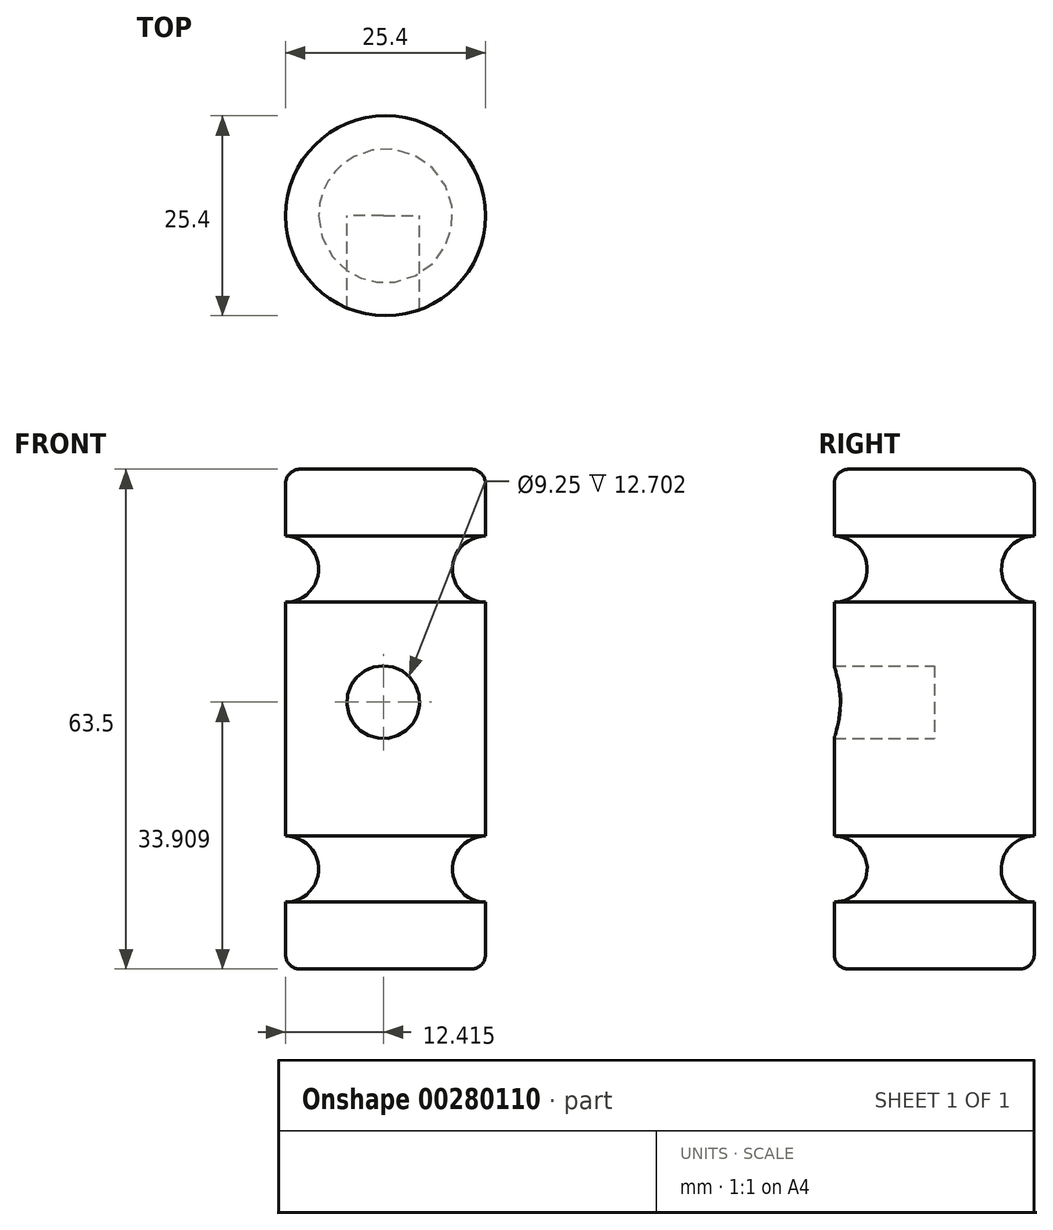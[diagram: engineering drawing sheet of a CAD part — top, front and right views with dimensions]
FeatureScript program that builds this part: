
annotation { "Feature Type Name" : "Feature", "Feature Type Description" : "" }
export const myFeature = defineFeature(function(context is Context, id is Id, definition is map)
    precondition{}
    {
        {
            var Q0;
            Q0=qCreatedBy(makeId("Front.planeOp"),FACE);
            var sketch = newSketch(context, id + "F0", { "sketchPlane" : qUnion([Q0])});
            skLineSegment(sketch, "E0.bottom", {"start": v(0, 0) * mm, "end": v(-12.7, 0) * mm});
            skLineSegment(sketch, "E0.top", {"start": v(0, 63.5) * mm, "end": v(-12.7, 63.5) * mm});
            skLineSegment(sketch, "E0.left", {"start": v(0, 0) * mm, "end": v(0, 8.5) * mm});
            skLineSegment(sketch, "E0.right", {"start": v(-12.7, 0) * mm, "end": v(-12.7, 63.5) * mm});
            skArc(sketch, "E1", {"start": v(0, 55) * mm, "mid": v(-4.2, 50.8) * mm, "end": v(0, 46.6) * mm});
            skArc(sketch, "E2", {"start": v(0, 16.9) * mm, "mid": v(-4.2, 12.7) * mm, "end": v(0, 8.5) * mm});
            skLineSegment(sketch, "E3.trimOffspring", {"start": v(0, 55) * mm, "end": v(0, 63.5) * mm});
            skLineSegment(sketch, "E4.trimOffspring", {"start": v(0, 16.9) * mm, "end": v(0, 46.6) * mm});
            skSolve(sketch);
        }
        {
            var Q0;
            Q0 = qSketchRegion(id + "F0", true);
            var Q1;
            Q1=sQuery(id+"F0.wireOp",EDGE,"E0.right");
            revolve(context, id + "F1", {"entities" : qUnion([Q0]), "axis" : qUnion([Q1]), "revolveType" : RevolveType.FULL});
        }
        {
            var Q0;
            Q0=makeQuery(id+"F1.opRevolve","SWEPT_EDGE",EDGE,{"disambiguationData":[OSD([sQuery(id+"F0.wireOp",EDGE,"E0.top"),sQuery(id+"F0.wireOp",EDGE,"E3.trimOffspring")])]});
            fillet(context, id + "F2", {"entities" : qUnion([Q0]), "radius" : 1.84 * mm, "tangentPropagation" : true, "allowEdgeOverflow" : false});
        }
        {
            var Q0;
            Q0=makeQuery(id+"F1.opRevolve","SWEPT_EDGE",EDGE,{"disambiguationData":[OSD([sQuery(id+"F0.wireOp",EDGE,"E0.bottom"),sQuery(id+"F0.wireOp",EDGE,"E0.left")])]});
            fillet(context, id + "F3", {"entities" : qUnion([Q0]), "radius" : 1.84 * mm, "tangentPropagation" : true, "allowEdgeOverflow" : false});
        }
        {
            var Q0;
            Q0=qCreatedBy(makeId("Front.planeOp"),FACE);
            var sketch = newSketch(context, id + "F4", { "sketchPlane" : qUnion([Q0])});
            skCircle(sketch, "E5", {"center": v(-12.98, 33.9) * mm, "radius": 4.62 * mm});
            skSolve(sketch);
        }
        {
            var Q0;
            Q0 = qSketchRegion(id + "F4", true);
            extrude(context, id + "F5", {"entities" : qUnion([Q0]), "operationType" : NewBodyOperationType.REMOVE, "depth" : 25.4 * mm});
        }
    });
